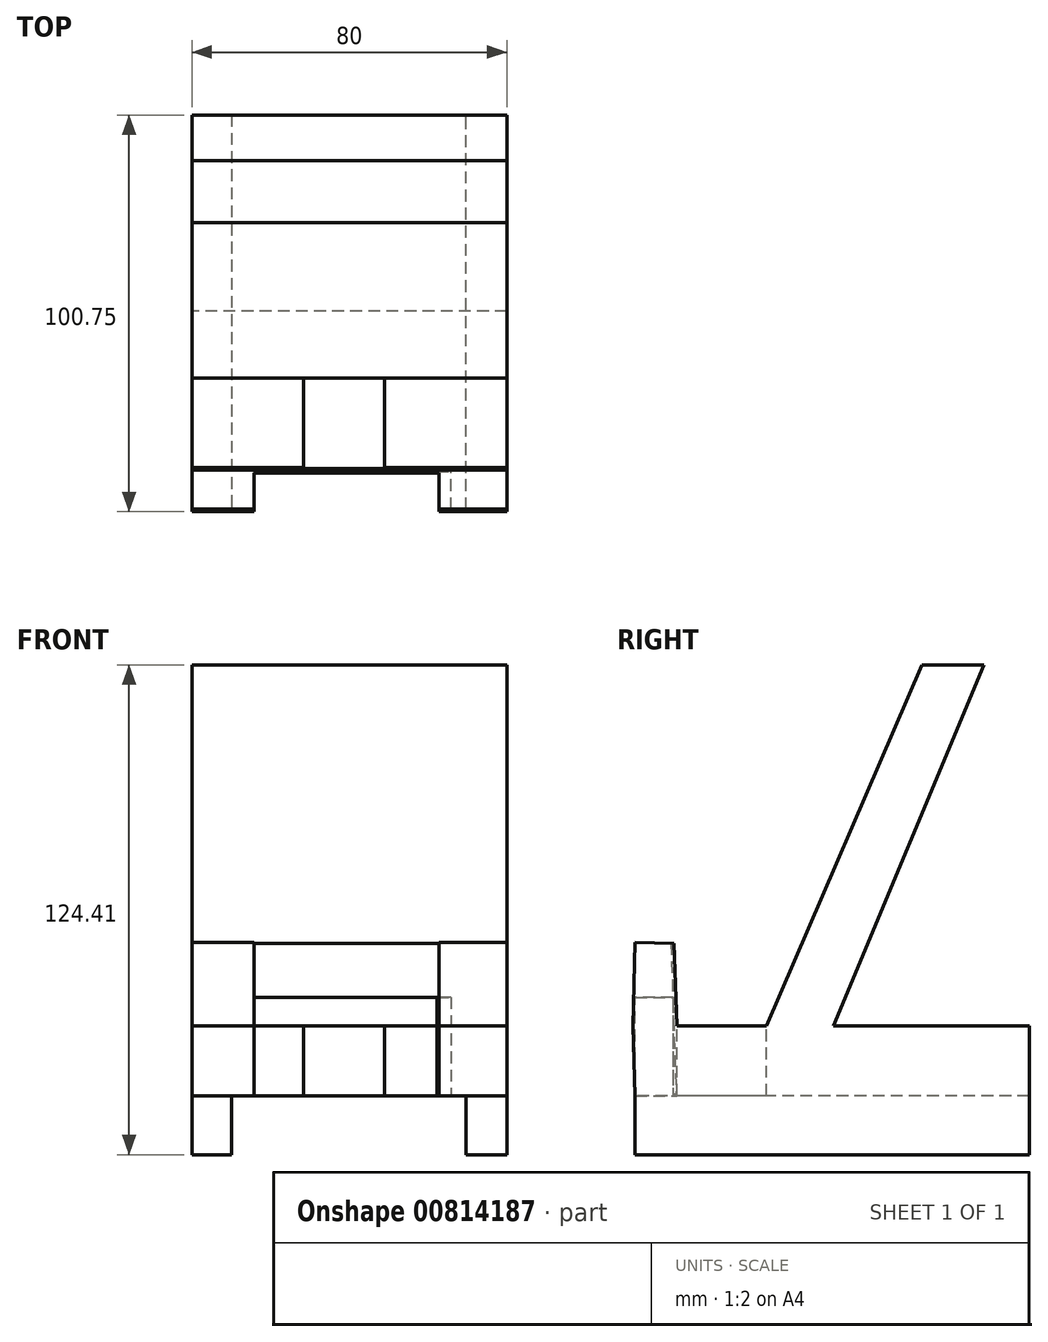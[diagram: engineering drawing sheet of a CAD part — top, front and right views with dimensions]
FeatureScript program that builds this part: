
annotation { "Feature Type Name" : "Feature", "Feature Type Description" : "" }
export const myFeature = defineFeature(function(context is Context, id is Id, definition is map)
    precondition{}
    {
        {
            var Q0;
            Q0=qCreatedBy(makeId("Right.planeOp"),FACE);
            var sketch = newSketch(context, id + "F0", { "sketchPlane" : qUnion([Q0])});
            skLineSegment(sketch, "E0", {"start": v(-50.37, 0) * mm, "end": v(49.79, 0) * mm});
            skLineSegment(sketch, "E1", {"start": v(49.79, 0) * mm, "end": v(49.79, 17.67) * mm});
            skLineSegment(sketch, "E2", {"start": v(49.79, 17.67) * mm, "end": v(-50.96, 17.67) * mm});
            skLineSegment(sketch, "E3", {"start": v(-50.96, 17.67) * mm, "end": v(-50.37, 0) * mm});
            skLineSegment(sketch, "E4", {"start": v(-50.96, 17.67) * mm, "end": v(-50.37, 38.98) * mm});
            skLineSegment(sketch, "E5", {"start": v(-50.37, 38.98) * mm, "end": v(-40.48, 38.71) * mm});
            skLineSegment(sketch, "E6", {"start": v(-40.48, 38.71) * mm, "end": v(-39.2, 0) * mm});
            skLineSegment(sketch, "E7", {"start": v(-39.2, 0) * mm, "end": v(-39.79, 17.67) * mm});
            skLineSegment(sketch, "E8", {"start": v(-39.79, 17.67) * mm, "end": v(-17.08, 17.67) * mm});
            skLineSegment(sketch, "E9", {"start": v(-17.08, 17.67) * mm, "end": v(22.43, 109.4) * mm});
            skLineSegment(sketch, "E10", {"start": v(22.43, 109.4) * mm, "end": v(38.24, 109.4) * mm});
            skLineSegment(sketch, "E11", {"start": v(38.24, 109.4) * mm, "end": v(0, 17.67) * mm});
            skSolve(sketch);
        }
        {
            var Q0;
            {var subQ0=sQuery(id+"F0.wireOp",EDGE,"E9");Q0=makeQuery(id+"F0.imprint","IMPRINT",FACE,{"disambiguationData":[TD([[makeQuery(id+"F0.imprint","IMPRINT",EDGE,{"derivedFrom":subQ0}),-1.0]])]});}
            var Q1;
            {var subQ4=sQuery(id+"F0.wireOp",EDGE,"E1");Q1=makeQuery(id+"F0.imprint","IMPRINT",FACE,{"disambiguationData":[TD([[makeQuery(id+"F0.imprint","IMPRINT",EDGE,{"derivedFrom":subQ4}),1.0]])]});}
            var Q2;
            {var subQ3=sQuery(id+"F0.wireOp",EDGE,"E3");Q2=makeQuery(id+"F0.imprint","IMPRINT",FACE,{"disambiguationData":[TD([[makeQuery(id+"F0.imprint","IMPRINT",EDGE,{"derivedFrom":subQ3}),1.0]])]});}
            var Q3;
            {var subQ0=sQuery(id+"F0.wireOp",EDGE,"E4");Q3=makeQuery(id+"F0.imprint","IMPRINT",FACE,{"disambiguationData":[TD([[makeQuery(id+"F0.imprint","IMPRINT",EDGE,{"derivedFrom":subQ0}),-1.0]])]});}
            extrude(context, id + "F1", {"entities" : qUnion([Q0, Q1, Q2, Q3]), "depth" : 80 * mm, "offsetDistance" : 25 * mm});
        }
        {
            var Q0;
            Q0=makeQuery(id+"F1.opExtrude","SWEPT_FACE",FACE,{"disambiguationData":[OSD([sQuery(id+"F0.wireOp",EDGE,"E0")])]});
            var sketch = newSketch(context, id + "F2", { "sketchPlane" : qUnion([Q0])});
            skLineSegment(sketch, "E12", {"start": v(0, 50.37) * mm, "end": v(0, -49.79) * mm});
            skLineSegment(sketch, "E13", {"start": v(0, -49.79) * mm, "end": v(10.12, -49.79) * mm});
            skLineSegment(sketch, "E14", {"start": v(10.12, -49.79) * mm, "end": v(10.12, 50.37) * mm});
            skLineSegment(sketch, "E15", {"start": v(10.12, 50.37) * mm, "end": v(0, 50.37) * mm});
            skLineSegment(sketch, "E16", {"start": v(80, 50.37) * mm, "end": v(69.6, 50.37) * mm});
            skLineSegment(sketch, "E17", {"start": v(69.6, 50.37) * mm, "end": v(69.6, -49.79) * mm});
            skLineSegment(sketch, "E18", {"start": v(69.6, -49.79) * mm, "end": v(80, -49.79) * mm});
            skLineSegment(sketch, "E19", {"start": v(80, -49.79) * mm, "end": v(80, 50.37) * mm});
            skSolve(sketch);
        }
        {
            var Q0;
            Q0=makeQuery(id+"F2.imprint","IMPRINT",FACE,{"disambiguationData":[TD([[makeQuery(id+"F2.imprint","IMPRINT",EDGE,{"derivedFrom":sQuery(id+"F2.wireOp",EDGE,"E12")}),1.0]])]});
            var Q1;
            Q1=makeQuery(id+"F2.imprint","IMPRINT",FACE,{"disambiguationData":[TD([[makeQuery(id+"F2.imprint","IMPRINT",EDGE,{"derivedFrom":sQuery(id+"F2.wireOp",EDGE,"E16")}),1.0]])]});
            extrude(context, id + "F3", {"entities" : qUnion([Q0, Q1]), "operationType" : NewBodyOperationType.ADD, "depth" : 15 * mm, "offsetDistance" : 25 * mm});
        }
        {
            var Q0;
            {var subQ0=sQuery(id+"F0.wireOp",EDGE,"E2");Q0=makeQuery(id+"F1.opExtrude","SWEPT_FACE",FACE,{"disambiguationData":[OSD([subQ0]),TDD([makeQuery(id+"F0.imprint","IMPRINT",EDGE,{"disambiguationData":[TD([[makeQuery(id+"F0.imprint","INTERSECT",VERTEX,{"derivedFrom":[subQ0,sQuery(id+"F0.wireOp",EDGE,"E9")]}),-1.0]])],"derivedFrom":subQ0})])]});}
            var sketch = newSketch(context, id + "F4", { "sketchPlane" : qUnion([Q0])});
            skLineSegment(sketch, "E20", {"start": v(29.66, -17.08) * mm, "end": v(29.66, -51.02) * mm});
            skLineSegment(sketch, "E21", {"start": v(29.66, -51.02) * mm, "end": v(45.18, -51.02) * mm});
            skLineSegment(sketch, "E22", {"start": v(45.18, -51.02) * mm, "end": v(45.18, -17.08) * mm});
            skLineSegment(sketch, "E23", {"start": v(45.18, -17.08) * mm, "end": v(29.66, -17.08) * mm});
            skSolve(sketch);
        }
        {
            var Q0;
            {var subQ0=sQuery(id+"F4.wireOp",EDGE,"E23");Q0=makeQuery(id+"F4.imprint","IMPRINT",FACE,{"disambiguationData":[TD([[makeQuery(id+"F4.imprint","IMPRINT",EDGE,{"derivedFrom":subQ0}),1.0]])]});}
            extrude(context, id + "F5", {"entities" : qUnion([Q0]), "operationType" : NewBodyOperationType.ADD, "oppositeDirection" : true, "depth" : 14.4 * mm, "offsetDistance" : 25 * mm});
        }
        {
            var Q0;
            {var subQ0=sQuery(id+"F0.wireOp",EDGE,"E2");Q0=makeQuery(id+"F1.opExtrude","SWEPT_FACE",FACE,{"disambiguationData":[OSD([subQ0]),TDD([makeQuery(id+"F0.imprint","IMPRINT",EDGE,{"disambiguationData":[TD([[makeQuery(id+"F0.imprint","INTERSECT",VERTEX,{"derivedFrom":[subQ0,sQuery(id+"F0.wireOp",EDGE,"E9")]}),-1.0]])],"derivedFrom":subQ0})])]});}
            var sketch = newSketch(context, id + "F6", { "sketchPlane" : qUnion([Q0])});
            skLineSegment(sketch, "E24.bottom", {"start": v(29.61, -17.08) * mm, "end": v(49.52, -17.08) * mm});
            skLineSegment(sketch, "E24.top", {"start": v(29.61, -39.79) * mm, "end": v(49.52, -39.79) * mm});
            skLineSegment(sketch, "E24.left", {"start": v(29.61, -17.08) * mm, "end": v(29.61, -39.79) * mm});
            skLineSegment(sketch, "E24.right", {"start": v(49.52, -17.08) * mm, "end": v(49.52, -39.79) * mm});
            skSolve(sketch);
        }
        {
            var Q0;
            Q0=makeQuery(id+"F6.imprint","IMPRINT",FACE,{"disambiguationData":[TD([[makeQuery(id+"F6.imprint","IMPRINT",EDGE,{"derivedFrom":sQuery(id+"F6.wireOp",EDGE,"E24.bottom")}),1.0]])]});
            extrude(context, id + "F7", {"entities" : qUnion([Q0]), "operationType" : NewBodyOperationType.ADD, "oppositeDirection" : true, "depth" : 17.6 * mm, "offsetDistance" : 25 * mm});
        }
        {
            var Q0;
            {var subQ0=sQuery(id+"F0.wireOp",EDGE,"E2");Q0=makeQuery(id+"F1.opExtrude","SWEPT_FACE",FACE,{"disambiguationData":[OSD([subQ0]),TDD([makeQuery(id+"F0.imprint","IMPRINT",EDGE,{"disambiguationData":[TD([[makeQuery(id+"F0.imprint","INTERSECT",VERTEX,{"derivedFrom":[subQ0,sQuery(id+"F0.wireOp",EDGE,"E9")]}),-1.0]])],"derivedFrom":subQ0})])]});}
            var sketch = newSketch(context, id + "F8", { "sketchPlane" : qUnion([Q0])});
            skLineSegment(sketch, "E25.bottom", {"start": v(28.37, -17.08) * mm, "end": v(48.96, -17.08) * mm});
            skLineSegment(sketch, "E25.top", {"start": v(28.37, -39.79) * mm, "end": v(48.96, -39.79) * mm});
            skLineSegment(sketch, "E25.left", {"start": v(28.37, -17.08) * mm, "end": v(28.37, -39.79) * mm});
            skLineSegment(sketch, "E25.right", {"start": v(48.96, -17.08) * mm, "end": v(48.96, -39.79) * mm});
            skSolve(sketch);
        }
        {
            var Q0;
            Q0=makeQuery(id+"F8.imprint","IMPRINT",FACE,{"disambiguationData":[TD([[makeQuery(id+"F8.imprint","IMPRINT",EDGE,{"derivedFrom":sQuery(id+"F8.wireOp",EDGE,"E25.bottom")}),1.0]])]});
            extrude(context, id + "F9", {"entities" : qUnion([Q0]), "operationType" : NewBodyOperationType.REMOVE, "oppositeDirection" : true, "depth" : 17.7 * mm, "offsetDistance" : 25 * mm});
        }
        {
            var Q0;
            Q0=makeQuery(id+"F1.opExtrude","SWEPT_FACE",FACE,{"disambiguationData":[OSD([sQuery(id+"F0.wireOp",EDGE,"E3")])]});
            var sketch = newSketch(context, id + "F10", { "sketchPlane" : qUnion([Q0])});
            skLineSegment(sketch, "E26.bottom", {"start": v(15.75, 41.33) * mm, "end": v(62.74, 41.33) * mm});
            skLineSegment(sketch, "E26.top", {"start": v(15.75, 1.66) * mm, "end": v(62.74, 1.66) * mm});
            skLineSegment(sketch, "E26.left", {"start": v(15.75, 41.33) * mm, "end": v(15.75, 1.66) * mm});
            skLineSegment(sketch, "E26.right", {"start": v(62.74, 41.33) * mm, "end": v(62.74, 1.66) * mm});
            skSolve(sketch);
        }
        {
            var Q0;
            {var subQ0=sQuery(id+"F10.wireOp",EDGE,"E26.top");Q0=makeQuery(id+"F10.imprint","IMPRINT",FACE,{"disambiguationData":[TD([[makeQuery(id+"F10.imprint","IMPRINT",EDGE,{"derivedFrom":subQ0}),-1.0]])]});}
            var Q1;
            {var subQ0=sQuery(id+"F10.wireOp",EDGE,"E26.bottom");Q1=makeQuery(id+"F10.imprint","IMPRINT",FACE,{"disambiguationData":[TD([[makeQuery(id+"F10.imprint","IMPRINT",EDGE,{"derivedFrom":subQ0}),-1.0]])]});}
            extrude(context, id + "F11", {"entities" : qUnion([Q0, Q1]), "operationType" : NewBodyOperationType.REMOVE, "oppositeDirection" : true, "depth" : 10.4 * mm, "offsetDistance" : 25 * mm});
        }
        {
            var Q0;
            Q0=makeQuery(id+"F1.opExtrude","SWEPT_FACE",FACE,{"disambiguationData":[OSD([sQuery(id+"F0.wireOp",EDGE,"E0")])]});
            var sketch = newSketch(context, id + "F12", { "sketchPlane" : qUnion([Q0])});
            skLineSegment(sketch, "E27.bottom", {"start": v(15.75, 50.37) * mm, "end": v(65.76, 50.37) * mm});
            skLineSegment(sketch, "E27.top", {"start": v(15.75, 40.76) * mm, "end": v(65.76, 40.76) * mm});
            skLineSegment(sketch, "E27.left", {"start": v(15.75, 50.37) * mm, "end": v(15.75, 40.76) * mm});
            skLineSegment(sketch, "E27.right", {"start": v(65.76, 50.37) * mm, "end": v(65.76, 40.76) * mm});
            skSolve(sketch);
        }
        {
            var Q0;
            Q0=makeQuery(id+"F12.imprint","IMPRINT",FACE,{"disambiguationData":[TD([[makeQuery(id+"F12.imprint","IMPRINT",EDGE,{"derivedFrom":sQuery(id+"F12.wireOp",EDGE,"E27.top")}),1.0]])]});
            extrude(context, id + "F13", {"entities" : qUnion([Q0]), "operationType" : NewBodyOperationType.REMOVE, "oppositeDirection" : true, "depth" : 25 * mm, "offsetDistance" : 25 * mm});
        }
        {
            var Q0;
            Q0=makeQuery(id+"F1.opExtrude","SWEPT_FACE",FACE,{"disambiguationData":[OSD([sQuery(id+"F0.wireOp",EDGE,"E0")])]});
            var sketch = newSketch(context, id + "F14", { "sketchPlane" : qUnion([Q0])});
            skPoint(sketch, "E28.oppositeSnap0", {"position": v(38.67, 39.79) * mm});
            skLineSegment(sketch, "E28.bottom", {"start": v(15.75, 40.76) * mm, "end": v(62.19, 40.76) * mm});
            skLineSegment(sketch, "E28.top", {"start": v(15.75, 39.79) * mm, "end": v(62.19, 39.79) * mm});
            skLineSegment(sketch, "E28.left", {"start": v(15.75, 40.76) * mm, "end": v(15.75, 39.79) * mm});
            skLineSegment(sketch, "E28.right", {"start": v(62.19, 40.76) * mm, "end": v(62.19, 39.79) * mm});
            skSolve(sketch);
        }
        {
            var Q0;
            Q0=makeQuery(id+"F14.imprint","IMPRINT",FACE,{"disambiguationData":[TD([[makeQuery(id+"F14.imprint","IMPRINT",EDGE,{"derivedFrom":sQuery(id+"F14.wireOp",EDGE,"E28.bottom")}),-1.0]])]});
            extrude(context, id + "F15", {"entities" : qUnion([Q0]), "operationType" : NewBodyOperationType.REMOVE, "oppositeDirection" : true, "depth" : 25 * mm, "offsetDistance" : 25 * mm});
        }
    });
